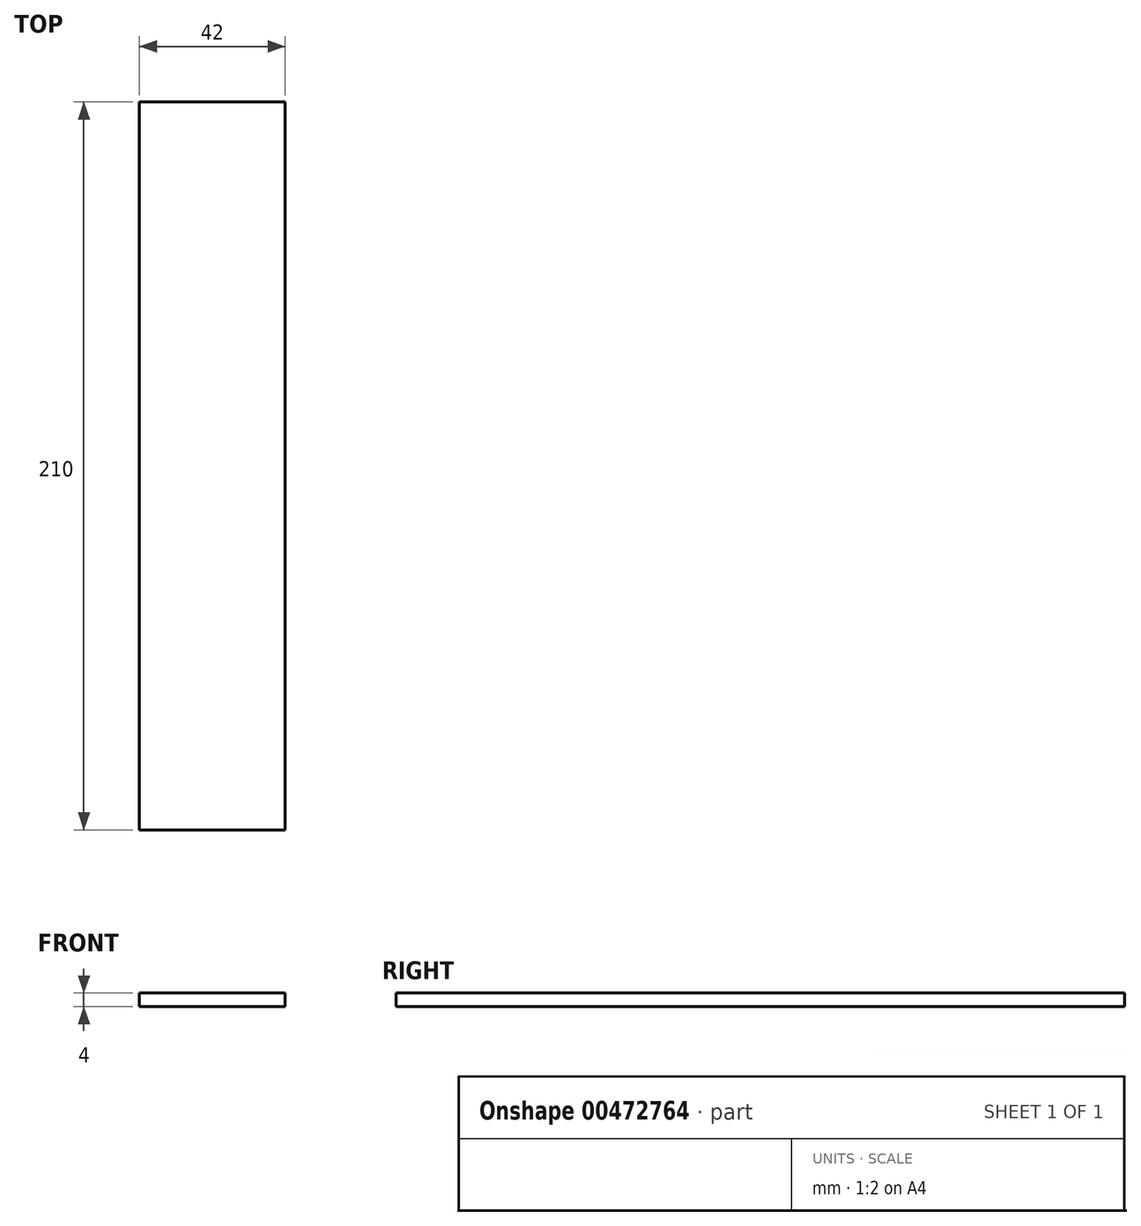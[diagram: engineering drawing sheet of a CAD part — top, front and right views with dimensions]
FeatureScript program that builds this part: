
annotation { "Feature Type Name" : "Feature", "Feature Type Description" : "" }
export const myFeature = defineFeature(function(context is Context, id is Id, definition is map)
    precondition{}
    {
        {
            assignVariable(context, id + "F0", {"name" : "e", "anyValue" : 4});
        }
        {
            var Q0;
            Q0=qCreatedBy(makeId("Top.planeOp"),FACE);
            var sketch = newSketch(context, id + "F1", { "sketchPlane" : qUnion([Q0])});
            skLineSegment(sketch, "E0.bottom", {"start": v(0, 0) * mm, "end": v(42, 0) * mm});
            skLineSegment(sketch, "E0.top", {"start": v(0, 210) * mm, "end": v(42, 210) * mm});
            skLineSegment(sketch, "E0.left", {"start": v(0, 0) * mm, "end": v(0, 210) * mm});
            skLineSegment(sketch, "E0.right", {"start": v(42, 0) * mm, "end": v(42, 210) * mm});
            skSolve(sketch);
        }
        {
            var Q0;
            Q0=makeQuery(id+"F1.imprint","IMPRINT",FACE,{"disambiguationData":[TD([[makeQuery(id+"F1.imprint","IMPRINT",EDGE,{"derivedFrom":sQuery(id+"F1.wireOp",EDGE,"E0.bottom")}),1.0]])]});
            extrude(context, id + "F2", {"entities" : qUnion([Q0]), "offsetDistance" : 25 * mm, "depth" : (getVariable(context, 'e')) * mm});
        }
    });
